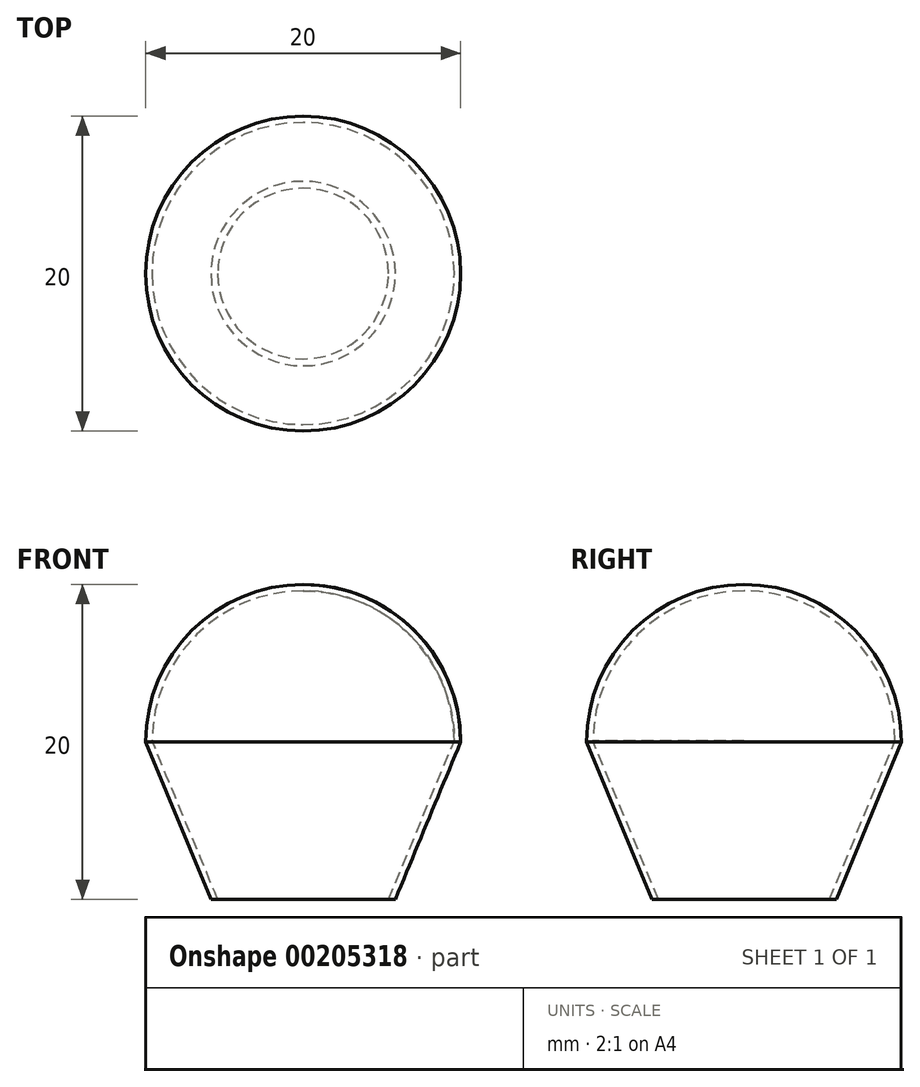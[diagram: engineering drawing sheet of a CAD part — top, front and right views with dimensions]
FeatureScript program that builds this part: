
annotation { "Feature Type Name" : "Feature", "Feature Type Description" : "" }
export const myFeature = defineFeature(function(context is Context, id is Id, definition is map)
    precondition{}
    {
        {
            var Q0;
            Q0=qCreatedBy(makeId("Top.planeOp"),FACE);
            var sketch = newSketch(context, id + "F0", { "sketchPlane" : qUnion([Q0])});
            skCircle(sketch, "E0", {"center": v(0, 0) * mm, "radius": 10 * mm});
            skSolve(sketch);
        }
        {
            var Q0;
            Q0=makeQuery(id+"F0.imprint","IMPRINT",FACE,{"disambiguationData":[TD([[makeQuery(id+"F0.imprint","IMPRINT",EDGE,{"derivedFrom":sQuery(id+"F0.wireOp",EDGE,"E0")}),1.0]])]});
            extrude(context, id + "F1", {"entities" : qUnion([Q0]), "oppositeDirection" : true, "depth" : 10 * mm, "offsetDistance" : 25 * mm, "hasDraft" : true, "draftAngle" : 22.5 * degree, "draftPullDirection" : true});
        }
        {
            var Q0;
            Q0=qCreatedBy(makeId("Front.planeOp"),FACE);
            var sketch = newSketch(context, id + "F2", { "sketchPlane" : qUnion([Q0])});
            skLineSegment(sketch, "E1", {"start": v(0, 0) * mm, "end": v(0, 10) * mm});
            skLineSegment(sketch, "E2", {"start": v(0, 0) * mm, "end": v(10, 0) * mm});
            skArc(sketch, "E3", {"start": v(10, 0) * mm, "mid": v(7.07, 7.07) * mm, "end": v(0, 10) * mm});
            skSolve(sketch);
        }
        {
            var Q0;
            Q0=makeQuery(id+"F2.imprint","IMPRINT",FACE,{"disambiguationData":[TD([[makeQuery(id+"F2.imprint","IMPRINT",EDGE,{"derivedFrom":sQuery(id+"F2.wireOp",EDGE,"E1")}),-1.0]])]});
            var Q1;
            Q1=makeQuery(id+"F1.opExtrude","CAP_EDGE",EDGE,{"disambiguationData":[OSD([sQuery(id+"F0.wireOp",EDGE,"E0")])],"isStart":false});
            revolve(context, id + "F3", {"operationType" : NewBodyOperationType.ADD, "surfaceOperationType" : NewSurfaceOperationType.NEW, "entities" : qUnion([Q0]), "axis" : qUnion([Q1]), "revolveType" : RevolveType.FULL});
        }
        {
            var Q0;
            Q0=makeQuery(id+"F1.opExtrude","CAP_FACE",FACE,{"disambiguationData":[OSD([sQuery(id+"F0.wireOp",EDGE,"E0")])],"isStart":false});
            shell(context, id + "F4", {"entities" : qUnion([Q0]), "thickness" : .4 * mm});
        }
    });
